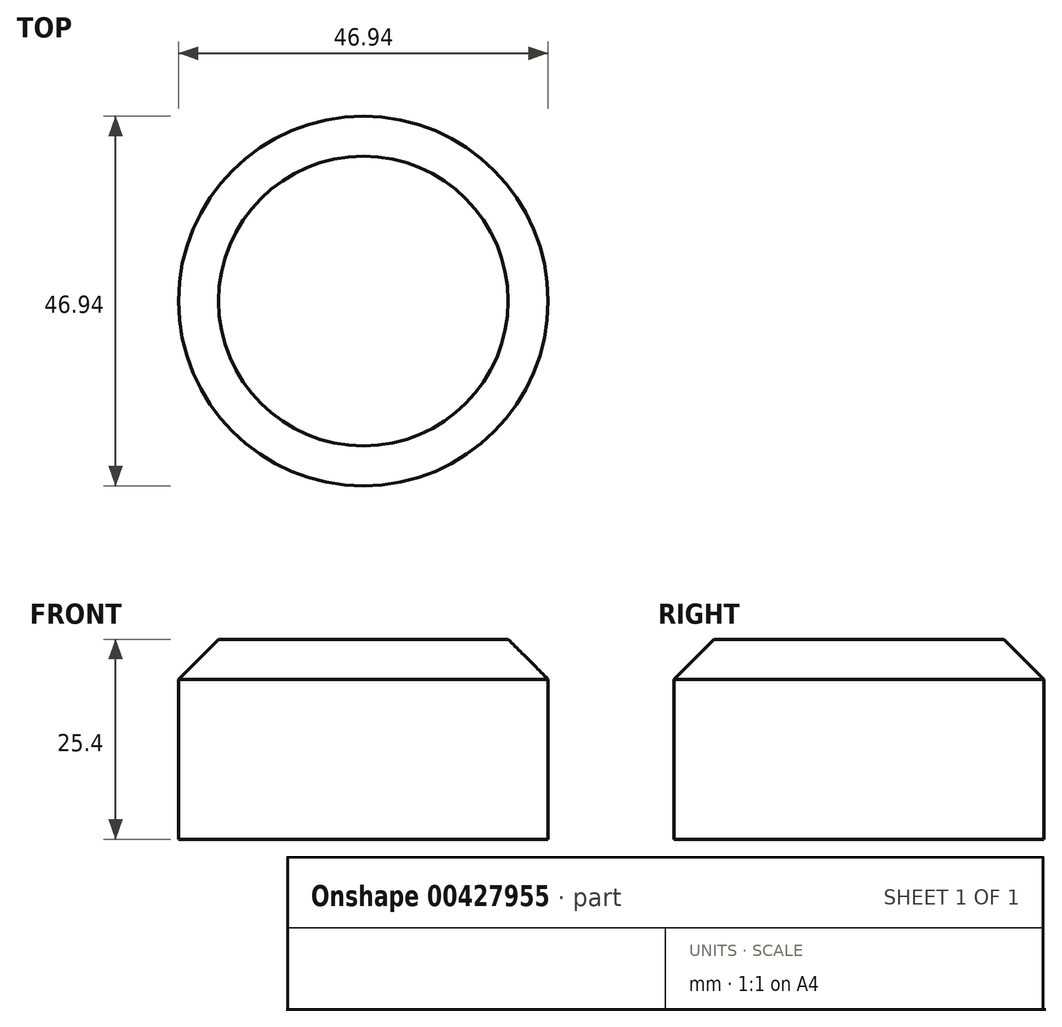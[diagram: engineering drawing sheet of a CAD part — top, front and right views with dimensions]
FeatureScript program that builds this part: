
annotation { "Feature Type Name" : "Feature", "Feature Type Description" : "" }
export const myFeature = defineFeature(function(context is Context, id is Id, definition is map)
    precondition{}
    {
        {
            var Q0;
            Q0=qCreatedBy(makeId("Top.planeOp"),FACE);
            var sketch = newSketch(context, id + "F0", { "sketchPlane" : qUnion([Q0])});
            skCircle(sketch, "E0", {"center": v(0, 0) * mm, "radius": 23.47 * mm});
            skSolve(sketch);
        }
        {
            var Q0;
            Q0 = qSketchRegion(id + "F0", true);
            extrude(context, id + "F1", {"entities" : qUnion([Q0]), "depth" : 25.4 * mm});
        }
        {
            var Q0;
            Q0=makeQuery(id+"F1.opExtrude","CAP_FACE",FACE,{"disambiguationData":[OSD([sQuery(id+"F0.wireOp",EDGE,"E0")])],"isStart":false});
            chamfer(context, id + "F2", {"entities" : qUnion([Q0]), "chamferType" : ChamferType.OFFSET_ANGLE, "width" : 5.08 * mm, "oppositeDirection" : false, "angle" : 45 * degree, "tangentPropagation" : true});
        }
    });
